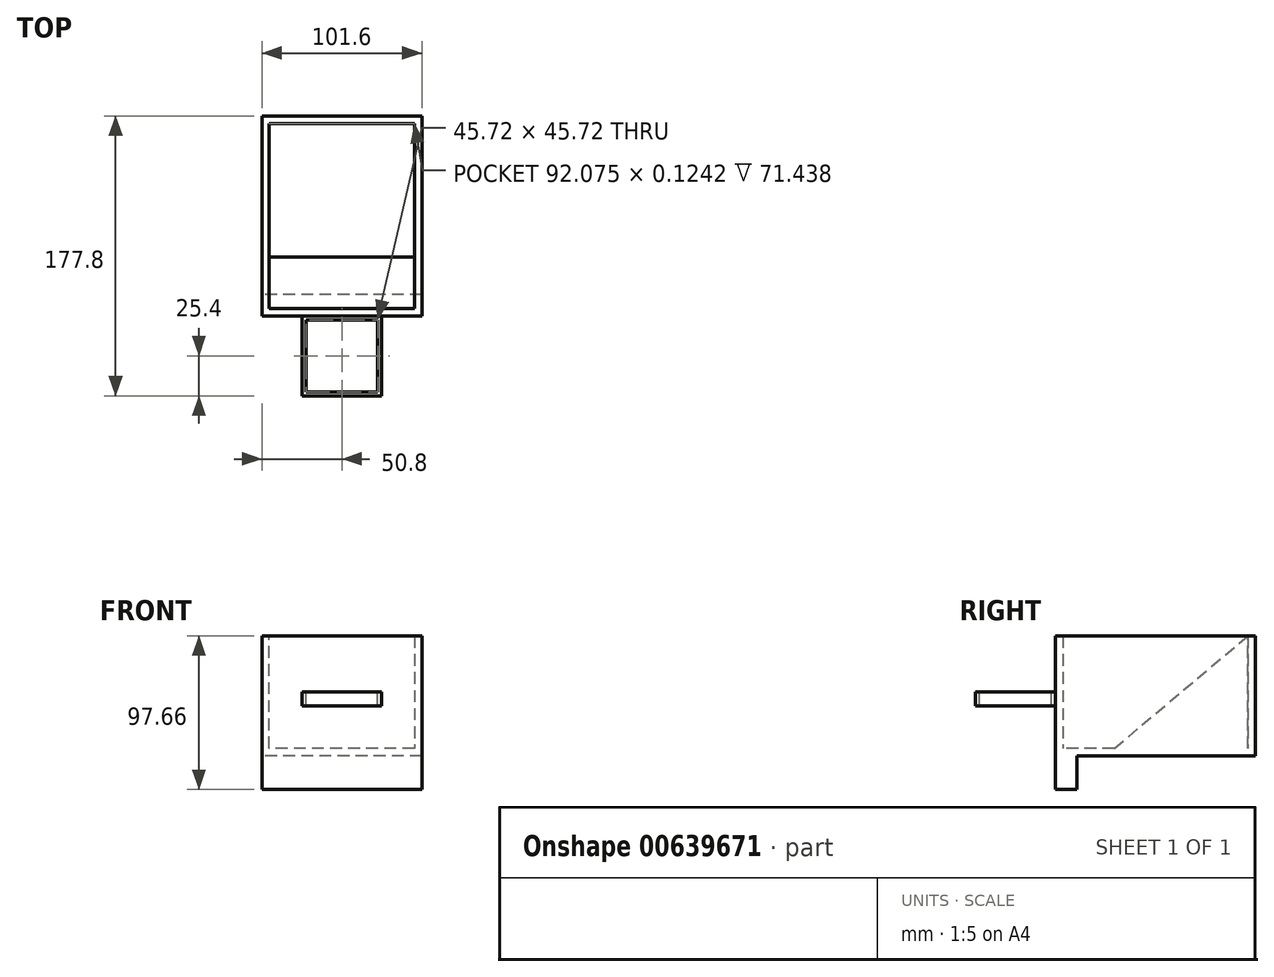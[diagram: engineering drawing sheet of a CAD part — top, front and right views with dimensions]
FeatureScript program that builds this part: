
annotation { "Feature Type Name" : "Feature", "Feature Type Description" : "" }
export const myFeature = defineFeature(function(context is Context, id is Id, definition is map)
    precondition{}
    {
        {
            var Q0;
            Q0=qCreatedBy(makeId("Front.planeOp"),FACE);
            var sketch = newSketch(context, id + "F0", { "sketchPlane" : qUnion([Q0])});
            skLineSegment(sketch, "E0", {"start": v(0, 0) * mm, "end": v(101.6, 0) * mm});
            skLineSegment(sketch, "E1", {"start": v(101.6, 0) * mm, "end": v(101.6, 76.2) * mm});
            skLineSegment(sketch, "E2", {"start": v(101.6, 76.2) * mm, "end": v(0, 76.2) * mm});
            skLineSegment(sketch, "E3", {"start": v(0, 76.2) * mm, "end": v(0, 0) * mm});
            skSolve(sketch);
        }
        {
            var Q0;
            Q0 = qSketchRegion(id + "F0", true);
            extrude(context, id + "F1", {"entities" : qUnion([Q0]), "oppositeDirection" : true, "depth" : 127 * mm, "offsetDistance" : 25.4 * mm});
        }
        {
            var Q0;
            Q0=makeQuery(id+"F1.opExtrude","SWEPT_FACE",FACE,{"disambiguationData":[OSD([sQuery(id+"F0.wireOp",EDGE,"E2")])]});
            shell(context, id + "F2", {"entities" : qUnion([Q0]), "thickness" : 4.76 * mm});
        }
        {
            var Q0;
            Q0=makeQuery(id+"F1.opExtrude","SWEPT_FACE",FACE,{"disambiguationData":[OSD([sQuery(id+"F0.wireOp",EDGE,"E1")])]});
            var sketch = newSketch(context, id + "F3", { "sketchPlane" : qUnion([Q0])});
            skLineSegment(sketch, "E4", {"start": v(122.11, 76.2) * mm, "end": v(31.75, 0) * mm});
            skLineSegment(sketch, "E5", {"start": v(122.11, 76.2) * mm, "end": v(122.11, 0) * mm});
            skLineSegment(sketch, "E6", {"start": v(122.11, 0) * mm, "end": v(31.75, 0) * mm});
            skSolve(sketch);
        }
        {
            var Q0;
            Q0=makeQuery(id+"F3.imprint","IMPRINT",FACE,{"disambiguationData":[TD([[makeQuery(id+"F3.imprint","IMPRINT",EDGE,{"derivedFrom":sQuery(id+"F3.wireOp",EDGE,"E4")}),1.0]])]});
            extrude(context, id + "F4", {"entities" : qUnion([Q0]), "operationType" : NewBodyOperationType.ADD, "oppositeDirection" : true, "depth" : 101.6 * mm, "offsetDistance" : 25.4 * mm});
        }
        {
            var Q0;
            Q0=makeQuery(id+"F1.opExtrude","CAP_FACE",FACE,{"disambiguationData":[OSD([sQuery(id+"F0.wireOp",EDGE,"E0"),sQuery(id+"F0.wireOp",EDGE,"E1"),sQuery(id+"F0.wireOp",EDGE,"E2"),sQuery(id+"F0.wireOp",EDGE,"E3")])],"isStart":true});
            var sketch = newSketch(context, id + "F5", { "sketchPlane" : qUnion([Q0])});
            skLineSegment(sketch, "E7", {"start": v(25.4, 40.64) * mm, "end": v(25.4, 31.75) * mm});
            skLineSegment(sketch, "E8", {"start": v(25.4, 31.75) * mm, "end": v(76.2, 31.75) * mm});
            skLineSegment(sketch, "E9", {"start": v(76.2, 31.75) * mm, "end": v(76.2, 40.64) * mm});
            skLineSegment(sketch, "E10", {"start": v(76.2, 40.64) * mm, "end": v(25.4, 40.64) * mm});
            skSolve(sketch);
        }
        {
            var Q0;
            Q0=makeQuery(id+"F5.imprint","IMPRINT",FACE,{"disambiguationData":[TD([[makeQuery(id+"F5.imprint","IMPRINT",EDGE,{"derivedFrom":sQuery(id+"F5.wireOp",EDGE,"E7")}),1.0]])]});
            extrude(context, id + "F6", {"entities" : qUnion([Q0]), "operationType" : NewBodyOperationType.ADD, "depth" : 50.8 * mm, "offsetDistance" : 25.4 * mm});
        }
        {
            var Q0;
            Q0=makeQuery(id+"F6.opExtrude","SWEPT_FACE",FACE,{"disambiguationData":[OSD([sQuery(id+"F5.wireOp",EDGE,"E10")])]});
            var sketch = newSketch(context, id + "F7", { "sketchPlane" : qUnion([Q0])});
            skLineSegment(sketch, "E11", {"start": v(27.94, -48.26) * mm, "end": v(27.94, -2.54) * mm});
            skLineSegment(sketch, "E12", {"start": v(27.94, -2.54) * mm, "end": v(73.66, -2.54) * mm});
            skLineSegment(sketch, "E13", {"start": v(73.66, -2.54) * mm, "end": v(73.66, -48.26) * mm});
            skLineSegment(sketch, "E14", {"start": v(73.66, -48.26) * mm, "end": v(27.94, -48.26) * mm});
            skSolve(sketch);
        }
        {
            var Q0;
            Q0=makeQuery(id+"F7.imprint","IMPRINT",FACE,{"disambiguationData":[TD([[makeQuery(id+"F7.imprint","IMPRINT",EDGE,{"derivedFrom":sQuery(id+"F7.wireOp",EDGE,"E11")}),-1.0]])]});
            extrude(context, id + "F8", {"entities" : qUnion([Q0]), "operationType" : NewBodyOperationType.REMOVE, "oppositeDirection" : true, "depth" : 25.4 * mm, "offsetDistance" : 25.4 * mm});
        }
        {
            var Q0;
            Q0=makeQuery(id+"F6.opExtrude","CAP_FACE",FACE,{"disambiguationData":[OSD([sQuery(id+"F5.wireOp",EDGE,"E7"),sQuery(id+"F5.wireOp",EDGE,"E8"),sQuery(id+"F5.wireOp",EDGE,"E9"),sQuery(id+"F5.wireOp",EDGE,"E10")])],"isStart":false});
            var sketch = newSketch(context, id + "F9", { "sketchPlane" : qUnion([Q0])});
            skCircle(sketch, "E15", {"center": v(51.74, 36.66) * mm, "radius": 4.15 * mm});
            skSolve(sketch);
        }
        {
            var Q0;
            Q0=sQuery(id+"F9.wireOp",EDGE,"E15");
            extrude(context, id + "F10", {"bodyType" : ToolBodyType.SURFACE, "surfaceEntities" : qUnion([Q0]), "depth" : 76.2 * mm, "offsetDistance" : 25.4 * mm});
        }
        {
            var Q0;
            Q0=qCreatedBy(makeId("Right.planeOp"),FACE);
            var sketch = newSketch(context, id + "F11", { "sketchPlane" : qUnion([Q0])});
            skLineSegment(sketch, "E16", {"start": v(0, 0) * mm, "end": v(13.59, 0) * mm});
            skLineSegment(sketch, "E17", {"start": v(13.59, 0) * mm, "end": v(13.59, -21.46) * mm});
            skLineSegment(sketch, "E18", {"start": v(13.59, -21.46) * mm, "end": v(0, -21.46) * mm});
            skLineSegment(sketch, "E19", {"start": v(0, -21.46) * mm, "end": v(0, 0) * mm});
            skSolve(sketch);
        }
        {
            var Q0;
            Q0=makeQuery(id+"F11.imprint","IMPRINT",FACE,{"disambiguationData":[TD([[makeQuery(id+"F11.imprint","IMPRINT",EDGE,{"derivedFrom":sQuery(id+"F11.wireOp",EDGE,"E16")}),-1.0]])]});
            extrude(context, id + "F12", {"entities" : qUnion([Q0]), "operationType" : NewBodyOperationType.ADD, "depth" : 101.6 * mm, "offsetDistance" : 25.4 * mm});
        }
    });
